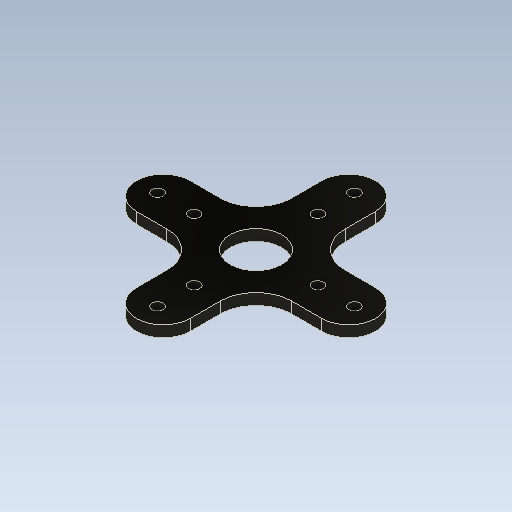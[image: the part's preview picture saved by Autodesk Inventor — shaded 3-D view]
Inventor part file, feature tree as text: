
AUTODESK INVENTOR PART (.ipt)
format: ipt  version: 2023 (Build 270158000, 158)  size: 143,872 bytes
history: native  units: in
note: dims shown in document units (in); Inventor stores cm internally (conversion verified against a paired STEP export)
features: other x3, sketch x1
ambient origin geometry x8: Origin, YZ Plane, XZ Plane, XY Plane, X Axis, Y Axis, Z Axis, Center Point
bodies: Solid1 (feature_tree)
feature tree (4):
  other  "DriveMotorPlate.ipt"
  other  "Solid1::DriveMotorPlate.ipt"
  other  "TaggingFeature1"
  sketch  "Sketch1"  dims[d0=0.3937in]
